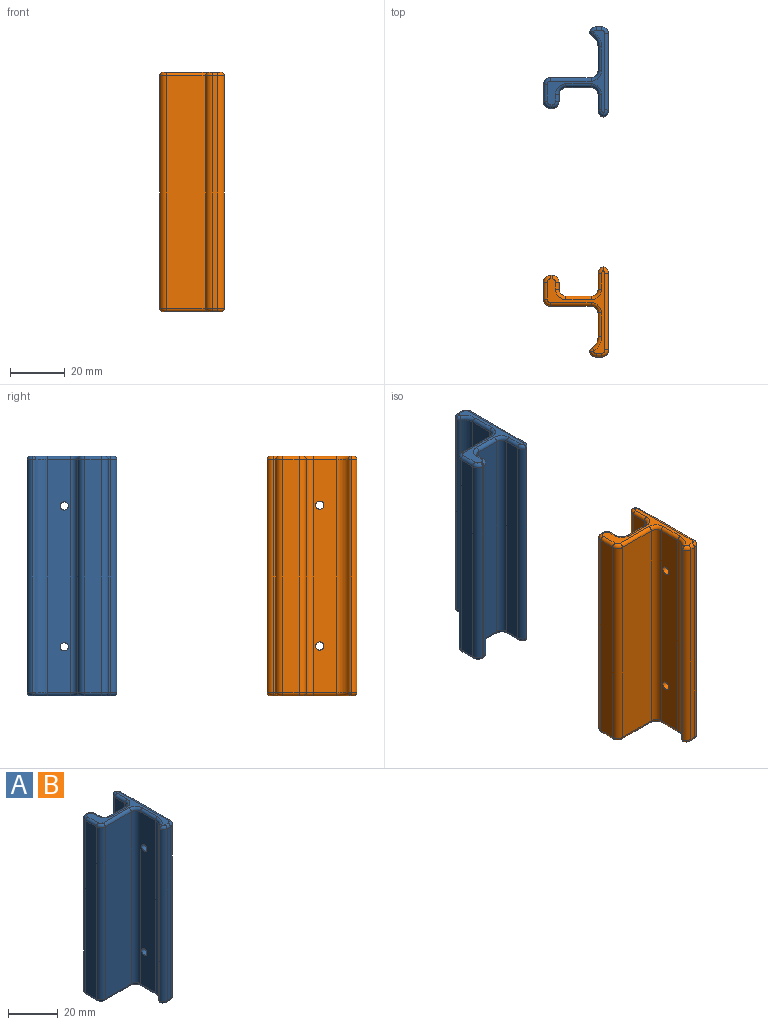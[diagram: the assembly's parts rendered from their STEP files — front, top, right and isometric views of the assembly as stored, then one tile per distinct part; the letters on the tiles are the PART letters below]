
ASSEMBLY  parts=2 mates=2
PART A: 67 faces, bbox 24.1x33.2x87.4 mm
  f0: plane 84.84x27.81mm, normal (1,0,0), area 2344.9mm2, adj f14,f17,f20,f21,f31,f53
  f1: plane 84.84x5.72mm, normal (-1,0,0), area 485.2mm2, adj f13,f22,f25,f47
  f2: plane 84.84x9.16mm, normal (0,1,0), area 776.7mm2, adj f22,f23,f28,f48
  f3: plane 84.84x2.53mm, normal (1,0,0), area 214.5mm2, adj f11,f23,f32,f52
  f4: plane 84.84x0.57mm, normal (0,1,0), area 47.9mm2, adj f11,f12,f36,f56
  f5: plane 84.84x6.09mm, normal (-1,0,0), area 516.4mm2, adj f12,f18,f40,f60
  f6: plane 84.84x14.8mm, normal (0,-1,0), area 1255.6mm2, adj f18,f24,f44,f64
  f7: plane 84.84x8.65mm, normal (-1,0,0), area 719.5mm2, adj f19,f20,f21,f24,f43,f65
  f8: plane 84.84x1.91mm, normal (0,-1,0), area 162.4mm2, adj f15,f17,f35,f57
  f9: plane 30.18x21.14mm, normal (0,0,1), area 96.2mm2, adj f46,f47,f48,f49,f50,f51,f52,f53
  f10: plane 30.18x21.14mm, normal (0,0,-1), area 96.2mm2, adj f25,f26,f27,f28,f29,f30,f31,f32
  f11: cylinder r=2.54mm len=84.84mm, axis (0,0,-1), area 338.5mm2, adj f3,f4,f34,f54
  f12: cylinder r=2.54mm len=84.84mm, axis (0,0,-1), area 338.5mm2, adj f4,f5,f38,f58
  f13: cylinder r=2.54mm len=84.84mm, axis (0,0,-1), area 283.8mm2, adj f1,f14,f27,f49
  f14: cylinder r=2.54mm len=84.84mm, axis (0,0,-1), area 283.8mm2, adj f0,f13,f29,f51
  f15: cylinder r=2.54mm len=84.84mm, axis (0,0,-1), area 278.4mm2, adj f8,f16,f37,f59
  f16: cylinder r=2.54mm len=84.84mm, axis (0,0,-1), area 144.7mm2, adj f15,f19,f39,f61
  f17: cylinder r=2.54mm len=84.84mm, axis (0,0,-1), area 338.5mm2, adj f0,f8,f33,f55
  f18: cylinder r=2.54mm len=84.84mm, axis (0,0,-1), area 338.5mm2, adj f5,f6,f42,f62
  f19: cylinder r=5.08mm len=84.84mm, axis (0,0,-1), area 409.6mm2, adj f7,f16,f41,f63
  f20: cylinder r=1.5mm len=3.8mm, axis (-1,0,0), area 35.9mm2, adj f0,f7
  f21: cylinder r=1.5mm len=3.8mm, axis (-1,0,0), area 35.9mm2, adj f0,f7
  f22: cylinder r=2.54mm len=84.84mm, axis (0,0,1), area 338.5mm2, adj f1,f2,f26,f46
  f23: cylinder r=2.54mm len=84.84mm, axis (0,0,1), area 338.5mm2, adj f2,f3,f30,f50
  f24: cylinder r=2.54mm len=84.84mm, axis (0,0,1), area 338.5mm2, adj f6,f7,f45,f66
  f25: cylinder r=1.27mm len=5.72mm, axis (0,-1,0), area 11.4mm2, adj f1,f10,f26,f27
  f26: torus R=3.81mm, axis (0,0,1), area 9.4mm2, adj f10,f22,f25,f28
  f27: torus R=1.27mm, axis (0,0,1), area 5.2mm2, adj f10,f13,f25,f29
  f28: cylinder r=1.27mm len=9.16mm, axis (-1,0,0), area 18.3mm2, adj f2,f10,f26,f30
  f29: torus R=1.27mm, axis (0,0,1), area 5.2mm2, adj f10,f14,f27,f31
  f30: torus R=3.81mm, axis (0,0,1), area 9.4mm2, adj f10,f23,f28,f32
  f31: cylinder r=1.27mm len=27.81mm, axis (0,1,0), area 55.5mm2, adj f0,f10,f29,f33
  f32: cylinder r=1.27mm len=2.53mm, axis (0,1,0), area 5mm2, adj f3,f10,f30,f34
  f33: torus R=1.27mm, axis (0,0,1), area 6.5mm2, adj f10,f17,f31,f35
  f34: torus R=1.27mm, axis (0,0,1), area 6.5mm2, adj f10,f11,f32,f36
  f35: cylinder r=1.27mm len=1.91mm, axis (1,0,0), area 3.8mm2, adj f8,f10,f33,f37
  f36: cylinder r=1.27mm len=1.27mm, axis (-1,0,0), area 1.1mm2, adj f4,f10,f34,f38
  f37: torus R=1.27mm, axis (0,0,1), area 5.1mm2, adj f10,f15,f35,f39
  f38: torus R=1.27mm, axis (0,0,1), area 6.5mm2, adj f10,f12,f36,f40
  f39: torus R=1.27mm, axis (0,0,1), area 2.5mm2, adj f10,f16,f37,f41
  f40: cylinder r=1.27mm len=6.09mm, axis (0,-1,0), area 12.1mm2, adj f5,f10,f38,f42
  f41: torus R=6.35mm, axis (0,0,1), area 10.5mm2, adj f10,f19,f39,f43
  f42: torus R=1.27mm, axis (0,0,1), area 6.5mm2, adj f10,f18,f40,f44
  f43: cylinder r=1.27mm len=8.65mm, axis (0,-1,0), area 17.3mm2, adj f7,f10,f41,f45
  f44: cylinder r=1.27mm len=14.8mm, axis (1,0,0), area 29.5mm2, adj f6,f10,f42,f45
  f45: torus R=3.81mm, axis (0,0,1), area 9.4mm2, adj f10,f24,f43,f44
  f46: torus R=3.81mm, axis (0,0,1), area 9.4mm2, adj f9,f22,f47,f48
  f47: cylinder r=1.27mm len=5.72mm, axis (0,1,0), area 11.4mm2, adj f1,f9,f46,f49
  f48: cylinder r=1.27mm len=9.16mm, axis (1,0,0), area 18.3mm2, adj f2,f9,f46,f50
  f49: torus R=1.27mm, axis (0,0,1), area 5.2mm2, adj f9,f13,f47,f51
  f50: torus R=3.81mm, axis (0,0,1), area 9.4mm2, adj f9,f23,f48,f52
  f51: torus R=1.27mm, axis (0,0,1), area 5.2mm2, adj f9,f14,f49,f53
  f52: cylinder r=1.27mm len=2.53mm, axis (0,-1,0), area 5mm2, adj f3,f9,f50,f54
  f53: cylinder r=1.27mm len=27.81mm, axis (0,-1,0), area 55.5mm2, adj f0,f9,f51,f55
  f54: torus R=1.27mm, axis (0,0,1), area 6.5mm2, adj f9,f11,f52,f56
  f55: torus R=1.27mm, axis (0,0,1), area 6.5mm2, adj f9,f17,f53,f57
  f56: cylinder r=1.27mm len=1.27mm, axis (1,0,0), area 1.1mm2, adj f4,f9,f54,f58
  f57: cylinder r=1.27mm len=1.91mm, axis (-1,0,0), area 3.8mm2, adj f8,f9,f55,f59
  f58: torus R=1.27mm, axis (0,0,1), area 6.5mm2, adj f9,f12,f56,f60
  f59: torus R=1.27mm, axis (0,0,1), area 5.1mm2, adj f9,f15,f57,f61
  f60: cylinder r=1.27mm len=6.09mm, axis (0,1,0), area 12.1mm2, adj f5,f9,f58,f62
  f61: torus R=1.27mm, axis (0,0,1), area 2.5mm2, adj f9,f16,f59,f63
  f62: torus R=1.27mm, axis (0,0,1), area 6.5mm2, adj f9,f18,f60,f64
  f63: torus R=6.35mm, axis (0,0,1), area 10.5mm2, adj f9,f19,f61,f65
  f64: cylinder r=1.27mm len=14.8mm, axis (-1,0,0), area 29.5mm2, adj f6,f9,f62,f66
  f65: cylinder r=1.27mm len=8.65mm, axis (0,1,0), area 17.3mm2, adj f7,f9,f63,f66
  f66: torus R=3.81mm, axis (0,0,1), area 9.4mm2, adj f9,f24,f64,f65
PART B: same geometry as A
PLACE A rot(axis=(1,0,0),180deg) t=(-29.74,80.87,72.89)mm
PLACE B t=(-29.74,-2.45,-14.49)mm fixed
MATE planar A.f18 <-> B.f9  axis (0,0,1) through (-50.88,78.33,72.89)mm
MATE planar A.f0 <-> B.f21  axis (1,0,0) through (-29.74,82.94,29.2)mm
